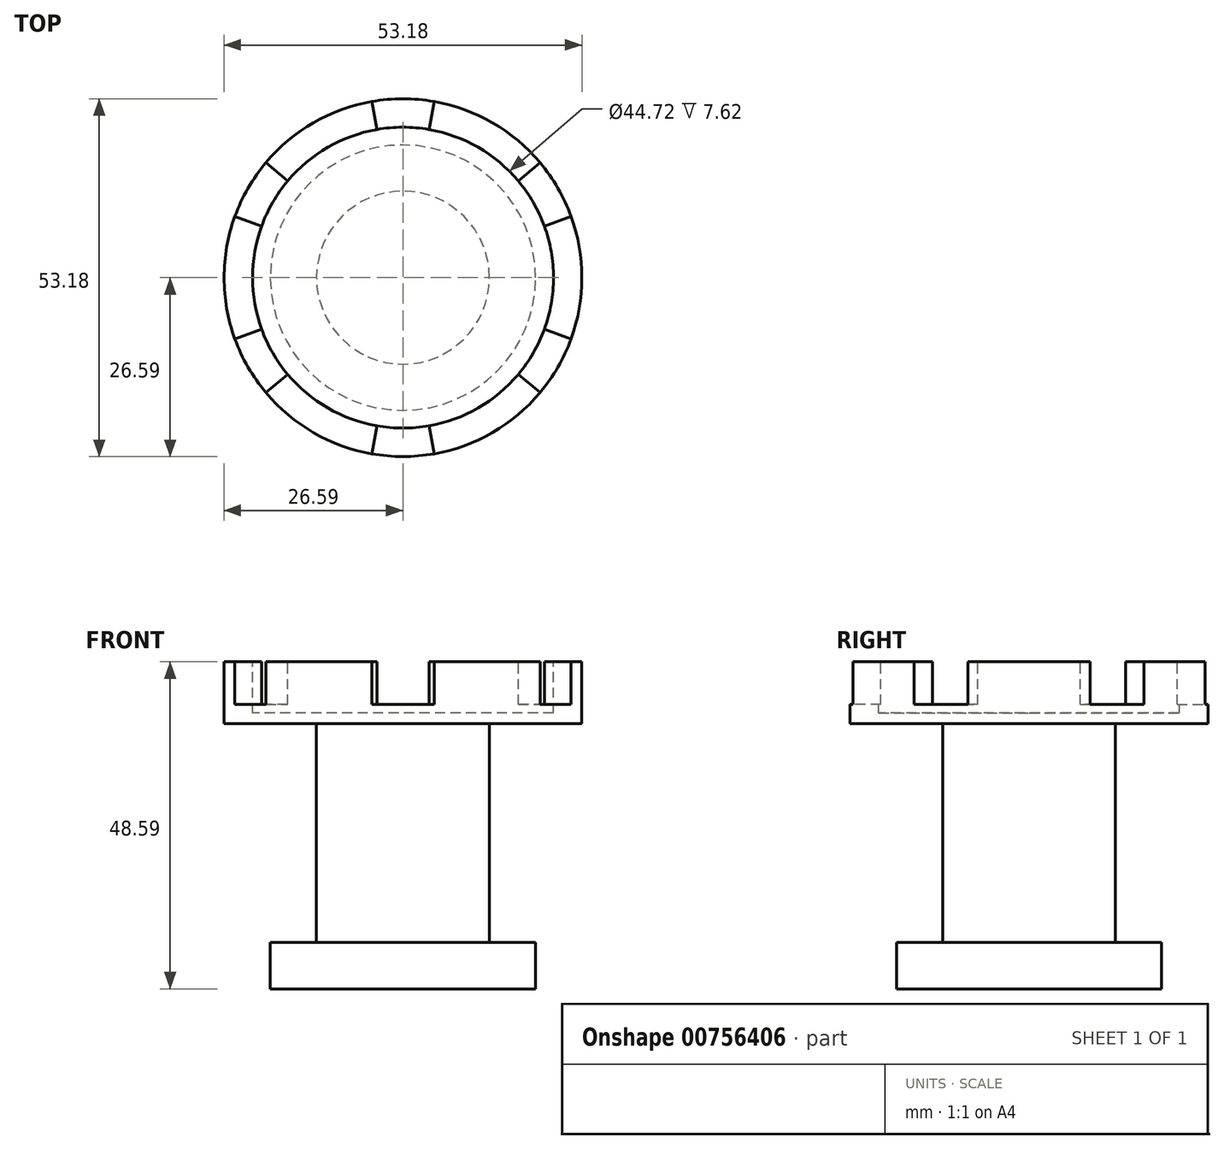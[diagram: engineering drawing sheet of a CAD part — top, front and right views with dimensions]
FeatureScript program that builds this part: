
annotation { "Feature Type Name" : "Feature", "Feature Type Description" : "" }
export const myFeature = defineFeature(function(context is Context, id is Id, definition is map)
    precondition{}
    {
        {
            var Q0;
            Q0=qCreatedBy(makeId("Front.planeOp"),FACE);
            var sketch = newSketch(context, id + "F0", { "sketchPlane" : qUnion([Q0])});
            skLineSegment(sketch, "E0.bottom", {"start": v(0, 0) * mm, "end": v(12.85, 0) * mm});
            skLineSegment(sketch, "E0.top", {"start": v(0, 39.43) * mm, "end": v(12.85, 39.43) * mm});
            skLineSegment(sketch, "E0.left", {"start": v(0, 0) * mm, "end": v(0, 39.43) * mm});
            skLineSegment(sketch, "E0.right", {"start": v(12.85, 0) * mm, "end": v(12.85, 39.43) * mm});
            skLineSegment(sketch, "E1.bottom", {"start": v(0, 39.43) * mm, "end": v(26.59, 39.43) * mm});
            skLineSegment(sketch, "E1.top", {"start": v(0, 48.6) * mm, "end": v(26.59, 48.6) * mm});
            skLineSegment(sketch, "E1.left", {"start": v(0, 39.43) * mm, "end": v(0, 48.6) * mm});
            skLineSegment(sketch, "E1.right", {"start": v(26.59, 39.43) * mm, "end": v(26.59, 48.6) * mm});
            skLineSegment(sketch, "E2.bottom", {"start": v(0, 0) * mm, "end": v(19.72, 0) * mm});
            skLineSegment(sketch, "E2.top", {"start": v(0, 6.87) * mm, "end": v(19.72, 6.87) * mm});
            skLineSegment(sketch, "E2.left", {"start": v(0, 0) * mm, "end": v(0, 6.87) * mm});
            skLineSegment(sketch, "E2.right", {"start": v(19.72, 0) * mm, "end": v(19.72, 6.87) * mm});
            skSolve(sketch);
        }
        {
            var Q0;
            Q0=makeQuery(id+"F0.imprint","IMPRINT",FACE,{"disambiguationData":[TD([[makeQuery(id+"F0.imprint","IMPRINT",EDGE,{"derivedFrom":sQuery(id+"F0.wireOp",EDGE,"E1.top")}),-1.0]])]});
            var Q1;
            {var subQ5=sQuery(id+"F0.wireOp",EDGE,"E2.right");Q1=makeQuery(id+"F0.imprint","IMPRINT",FACE,{"disambiguationData":[TD([[makeQuery(id+"F0.imprint","IMPRINT",EDGE,{"derivedFrom":subQ5}),1.0]])]});}
            var Q2;
            {var subQ0=sQuery(id+"F0.wireOp",EDGE,"E0.left");Q2=makeQuery(id+"F0.imprint","IMPRINT",FACE,{"disambiguationData":[TD([[makeQuery(id+"F0.imprint","IMPRINT",EDGE,{"derivedFrom":subQ0}),-1.0]])]});}
            var Q3;
            {var subQ5=sQuery(id+"F0.wireOp",EDGE,"E2.left");Q3=makeQuery(id+"F0.imprint","IMPRINT",FACE,{"disambiguationData":[TD([[makeQuery(id+"F0.imprint","IMPRINT",EDGE,{"derivedFrom":subQ5}),-1.0]])]});}
            var Q4;
            Q4=sQuery(id+"F0.wireOp",EDGE,"E0.left");
            revolve(context, id + "F1", {"surfaceOperationType" : NewSurfaceOperationType.NEW, "entities" : qUnion([Q0, Q1, Q2, Q3]), "axis" : qUnion([Q4]), "revolveType" : RevolveType.FULL});
        }
        {
            var Q0;
            Q0=makeQuery(id+"F1.opRevolve","SWEPT_FACE",FACE,{"disambiguationData":[OSD([sQuery(id+"F0.wireOp",EDGE,"E1.top")])]});
            var sketch = newSketch(context, id + "F2", { "sketchPlane" : qUnion([Q0])});
            skCircle(sketch, "E3", {"center": v(0, 0) * mm, "radius": 22.36 * mm});
            skSolve(sketch);
        }
        {
            var Q0;
            Q0=makeQuery(id+"F2.imprint","IMPRINT",FACE,{"disambiguationData":[TD([[makeQuery(id+"F2.imprint","IMPRINT",EDGE,{"derivedFrom":sQuery(id+"F2.wireOp",EDGE,"E3")}),1.0]])]});
            extrude(context, id + "F3", {"entities" : qUnion([Q0]), "operationType" : NewBodyOperationType.REMOVE, "oppositeDirection" : true, "depth" : 7.62 * mm, "offsetDistance" : 25.4 * mm});
        }
        {
            var Q0;
            Q0=makeQuery(id+"F1.opRevolve","SWEPT_FACE",FACE,{"disambiguationData":[OSD([sQuery(id+"F0.wireOp",EDGE,"E1.top")])]});
            var sketch = newSketch(context, id + "F4", { "sketchPlane" : qUnion([Q0])});
            skLineSegment(sketch, "E4", {"start": v(3.05, 17.3) * mm, "end": v(5.44, 30.85) * mm});
            skLineSegment(sketch, "E5", {"start": v(-3.05, 17.3) * mm, "end": v(-5.44, 30.85) * mm});
            skArc(sketch, "E6", {"start": v(5.44, 30.85) * mm, "mid": v(0, 31.33) * mm, "end": v(-5.44, 30.85) * mm});
            skArc(sketch, "E7", {"start": v(3.05, 17.3) * mm, "mid": v(0, 17.57) * mm, "end": v(-3.05, 17.3) * mm});
            skArc(sketch, "E8.1.0", {"start": v(-13.46, 11.3) * mm, "mid": v(-15.22, 8.79) * mm, "end": v(-16.51, 6.01) * mm});
            skLineSegment(sketch, "E8.1.1", {"start": v(-16.51, 6.01) * mm, "end": v(-29.44, 10.72) * mm});
            skArc(sketch, "E8.1.2", {"start": v(-24, 20.14) * mm, "mid": v(-27.13, 15.66) * mm, "end": v(-29.44, 10.72) * mm});
            skLineSegment(sketch, "E8.1.3", {"start": v(-13.46, 11.3) * mm, "end": v(-24, 20.14) * mm});
            skArc(sketch, "E8.2.0", {"start": v(-16.51, -6.01) * mm, "mid": v(-15.22, -8.79) * mm, "end": v(-13.46, -11.3) * mm});
            skLineSegment(sketch, "E8.2.1", {"start": v(-13.46, -11.3) * mm, "end": v(-24, -20.14) * mm});
            skArc(sketch, "E8.2.2", {"start": v(-29.44, -10.72) * mm, "mid": v(-27.13, -15.66) * mm, "end": v(-24, -20.14) * mm});
            skLineSegment(sketch, "E8.2.3", {"start": v(-16.51, -6.01) * mm, "end": v(-29.44, -10.72) * mm});
            skArc(sketch, "E8.3.0", {"start": v(-3.05, -17.3) * mm, "mid": v(0, -17.57) * mm, "end": v(3.05, -17.3) * mm});
            skLineSegment(sketch, "E8.3.1", {"start": v(3.05, -17.3) * mm, "end": v(5.44, -30.85) * mm});
            skArc(sketch, "E8.3.2", {"start": v(-5.44, -30.85) * mm, "mid": v(0, -31.33) * mm, "end": v(5.44, -30.85) * mm});
            skLineSegment(sketch, "E8.3.3", {"start": v(-3.05, -17.3) * mm, "end": v(-5.44, -30.85) * mm});
            skArc(sketch, "E8.4.0", {"start": v(13.46, -11.3) * mm, "mid": v(15.22, -8.79) * mm, "end": v(16.51, -6.01) * mm});
            skLineSegment(sketch, "E8.4.1", {"start": v(16.51, -6.01) * mm, "end": v(29.44, -10.72) * mm});
            skArc(sketch, "E8.4.2", {"start": v(24, -20.14) * mm, "mid": v(27.13, -15.66) * mm, "end": v(29.44, -10.72) * mm});
            skLineSegment(sketch, "E8.4.3", {"start": v(13.46, -11.3) * mm, "end": v(24, -20.14) * mm});
            skArc(sketch, "E8.5.0", {"start": v(16.51, 6.01) * mm, "mid": v(15.22, 8.79) * mm, "end": v(13.46, 11.3) * mm});
            skLineSegment(sketch, "E8.5.1", {"start": v(13.46, 11.3) * mm, "end": v(24, 20.14) * mm});
            skArc(sketch, "E8.5.2", {"start": v(29.44, 10.72) * mm, "mid": v(27.13, 15.66) * mm, "end": v(24, 20.14) * mm});
            skLineSegment(sketch, "E8.5.3", {"start": v(16.51, 6.01) * mm, "end": v(29.44, 10.72) * mm});
            skSolve(sketch);
        }
        {
            var Q0;
            Q0 = qSketchRegion(id + "F4", true);
            extrude(context, id + "F5", {"entities" : qUnion([Q0]), "operationType" : NewBodyOperationType.REMOVE, "oppositeDirection" : true, "depth" : 6.35 * mm, "offsetDistance" : 25.4 * mm});
        }
    });
